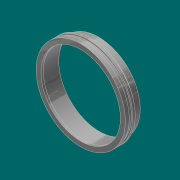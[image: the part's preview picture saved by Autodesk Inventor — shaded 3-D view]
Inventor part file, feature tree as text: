
AUTODESK INVENTOR PART (.ipt)
format: ipt  version: 2017.3 (Build 213256000, 256)  size: 160,768 bytes
history: native  units: in
note: dims shown in document units (in); Inventor stores cm internally (conversion verified against a paired STEP export)
features: revolve x1, chamfer x1, sketch x1
ambient origin geometry x8: Origin, YZ Plane, XZ Plane, XY Plane, X Axis, Y Axis, Z Axis, Center Point
bodies: Solid1 (feature_tree)
feature tree (3):
  revolve  "Revolution1"  [1 undecoded]
  chamfer  "Chamfer2"  Angle=90.0deg  [1 undecoded]
  sketch  "Sketch1"  dims[d0=17.125in d5=1.0in d6=90.0deg d13=18.75in d14=19.25in d16=1.75in d17=1.35in d18=0.0515in d19=0.0842in d20=0.0312in d21=0.125in d22=45.0deg d32=18.0in d33=0.4375in d35=0.0625in d36=0.25in d38=8.0in d43=4.25in d44=0.5in d45=60.0deg d46=0.2577in]
note: 2 required parameter values undecoded (feature->parameter linkage not recoverable at this tier; creation-order binding heuristic only, values carry confidence <= 0.55)